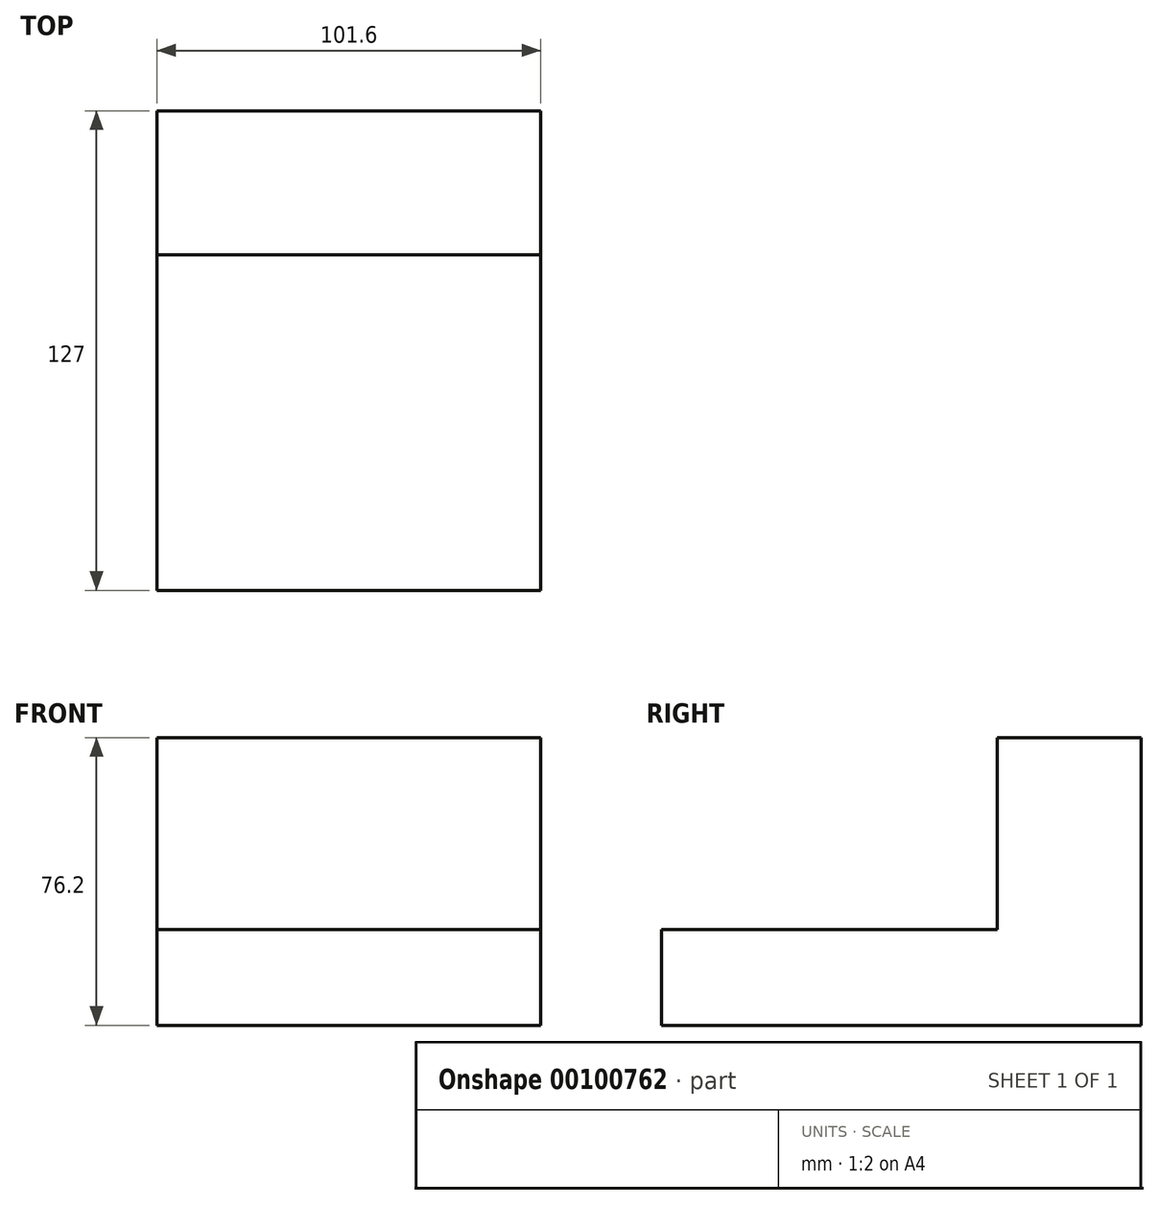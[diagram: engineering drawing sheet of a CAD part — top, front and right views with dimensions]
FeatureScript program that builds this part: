
annotation { "Feature Type Name" : "Feature", "Feature Type Description" : "" }
export const myFeature = defineFeature(function(context is Context, id is Id, definition is map)
    precondition{}
    {
        {
            var Q0;
            Q0=qCreatedBy(makeId("Top.planeOp"),FACE);
            var sketch = newSketch(context, id + "F0", { "sketchPlane" : qUnion([Q0])});
            skLineSegment(sketch, "E0.bottom", {"start": v(-47.58, 64.99) * mm, "end": v(54.02, 64.99) * mm});
            skLineSegment(sketch, "E0.top", {"start": v(-47.58, -62.01) * mm, "end": v(54.02, -62.01) * mm});
            skLineSegment(sketch, "E0.left", {"start": v(-47.58, 64.99) * mm, "end": v(-47.58, -62.01) * mm});
            skLineSegment(sketch, "E0.right", {"start": v(54.02, 64.99) * mm, "end": v(54.02, -62.01) * mm});
            skSolve(sketch);
        }
        {
            var Q0;
            Q0=makeQuery(id+"F0.imprint","IMPRINT",FACE,{"disambiguationData":[TD([[makeQuery(id+"F0.imprint","IMPRINT",EDGE,{"derivedFrom":sQuery(id+"F0.wireOp",EDGE,"E0.bottom")}),-1.0]])]});
            extrude(context, id + "F1", {"entities" : qUnion([Q0]), "depth" : 25.4 * mm});
        }
        {
            var Q0;
            Q0=makeQuery(id+"F1.opExtrude","CAP_FACE",FACE,{"disambiguationData":[OSD([sQuery(id+"F0.wireOp",EDGE,"E0.bottom"),sQuery(id+"F0.wireOp",EDGE,"E0.top"),sQuery(id+"F0.wireOp",EDGE,"E0.left"),sQuery(id+"F0.wireOp",EDGE,"E0.right")])],"isStart":false});
            var sketch = newSketch(context, id + "F2", { "sketchPlane" : qUnion([Q0])});
            skLineSegment(sketch, "E1.bottom", {"start": v(-47.58, 64.99) * mm, "end": v(54.02, 64.99) * mm});
            skLineSegment(sketch, "E1.top", {"start": v(-47.58, 26.89) * mm, "end": v(54.02, 26.89) * mm});
            skLineSegment(sketch, "E1.left", {"start": v(-47.58, 64.99) * mm, "end": v(-47.58, 26.89) * mm});
            skLineSegment(sketch, "E1.right", {"start": v(54.02, 64.99) * mm, "end": v(54.02, 26.89) * mm});
            skLineSegment(sketch, "E2.bottom", {"start": v(-47.58, 26.89) * mm, "end": v(-22.18, 26.89) * mm});
            skLineSegment(sketch, "E2.top", {"start": v(-47.58, -11.21) * mm, "end": v(-22.18, -11.21) * mm});
            skLineSegment(sketch, "E2.left", {"start": v(-47.58, 26.89) * mm, "end": v(-47.58, -11.21) * mm});
            skLineSegment(sketch, "E2.right", {"start": v(-22.18, 26.89) * mm, "end": v(-22.18, -11.21) * mm});
            skLineSegment(sketch, "E3.bottom", {"start": v(54.02, 26.89) * mm, "end": v(28.62, 26.89) * mm});
            skLineSegment(sketch, "E3.top", {"start": v(54.02, -11.21) * mm, "end": v(28.62, -11.21) * mm});
            skLineSegment(sketch, "E3.left", {"start": v(54.02, 26.89) * mm, "end": v(54.02, -11.21) * mm});
            skLineSegment(sketch, "E3.right", {"start": v(28.62, 26.89) * mm, "end": v(28.62, -11.21) * mm});
            skSolve(sketch);
        }
        {
            var Q0;
            Q0=makeQuery(id+"F2.imprint","IMPRINT",FACE,{"disambiguationData":[TD([[makeQuery(id+"F2.imprint","IMPRINT",EDGE,{"derivedFrom":sQuery(id+"F2.wireOp",EDGE,"E1.bottom")}),-1.0]])]});
            var Q1;
            Q1=makeQuery(id+"F2.imprint","IMPRINT",FACE,{"disambiguationData":[TD([[makeQuery(id+"F2.imprint","IMPRINT",EDGE,{"derivedFrom":sQuery(id+"F2.wireOp",EDGE,"E2.bottom")}),-1.0]])]});
            var Q2;
            Q2=makeQuery(id+"F2.imprint","IMPRINT",FACE,{"disambiguationData":[TD([[makeQuery(id+"F2.imprint","IMPRINT",EDGE,{"derivedFrom":sQuery(id+"F2.wireOp",EDGE,"E3.bottom")}),1.0]])]});
            extrude(context, id + "F3", {"entities" : qUnion([Q0, Q1, Q2]), "operationType" : NewBodyOperationType.ADD, "depth" : 25.4 * mm});
        }
        {
            var Q0;
            Q0=makeQuery(id+"F3.opExtrude","CAP_FACE",FACE,{"disambiguationData":[OSD([sQuery(id+"F2.wireOp",EDGE,"E1.bottom"),sQuery(id+"F2.wireOp",EDGE,"E1.top"),sQuery(id+"F2.wireOp",EDGE,"E1.left"),sQuery(id+"F2.wireOp",EDGE,"E1.right"),sQuery(id+"F2.wireOp",EDGE,"E2.top"),sQuery(id+"F2.wireOp",EDGE,"E2.left"),sQuery(id+"F2.wireOp",EDGE,"E2.right"),sQuery(id+"F2.wireOp",EDGE,"E3.top"),sQuery(id+"F2.wireOp",EDGE,"E3.left"),sQuery(id+"F2.wireOp",EDGE,"E3.right")])],"isStart":false});
            var sketch = newSketch(context, id + "F4", { "sketchPlane" : qUnion([Q0])});
            skLineSegment(sketch, "E4.bottom", {"start": v(-47.58, 64.99) * mm, "end": v(54.02, 64.99) * mm});
            skLineSegment(sketch, "E4.top", {"start": v(-47.58, 26.89) * mm, "end": v(54.02, 26.89) * mm});
            skLineSegment(sketch, "E4.left", {"start": v(-47.58, 64.99) * mm, "end": v(-47.58, 26.89) * mm});
            skLineSegment(sketch, "E4.right", {"start": v(54.02, 64.99) * mm, "end": v(54.02, 26.89) * mm});
            skSolve(sketch);
        }
        {
            var Q0;
            Q0=makeQuery(id+"F4.imprint","IMPRINT",FACE,{"disambiguationData":[TD([[makeQuery(id+"F4.imprint","IMPRINT",EDGE,{"derivedFrom":sQuery(id+"F4.wireOp",EDGE,"E4.bottom")}),-1.0]])]});
            extrude(context, id + "F5", {"entities" : qUnion([Q0]), "operationType" : NewBodyOperationType.ADD, "depth" : 25.4 * mm});
        }
    });
